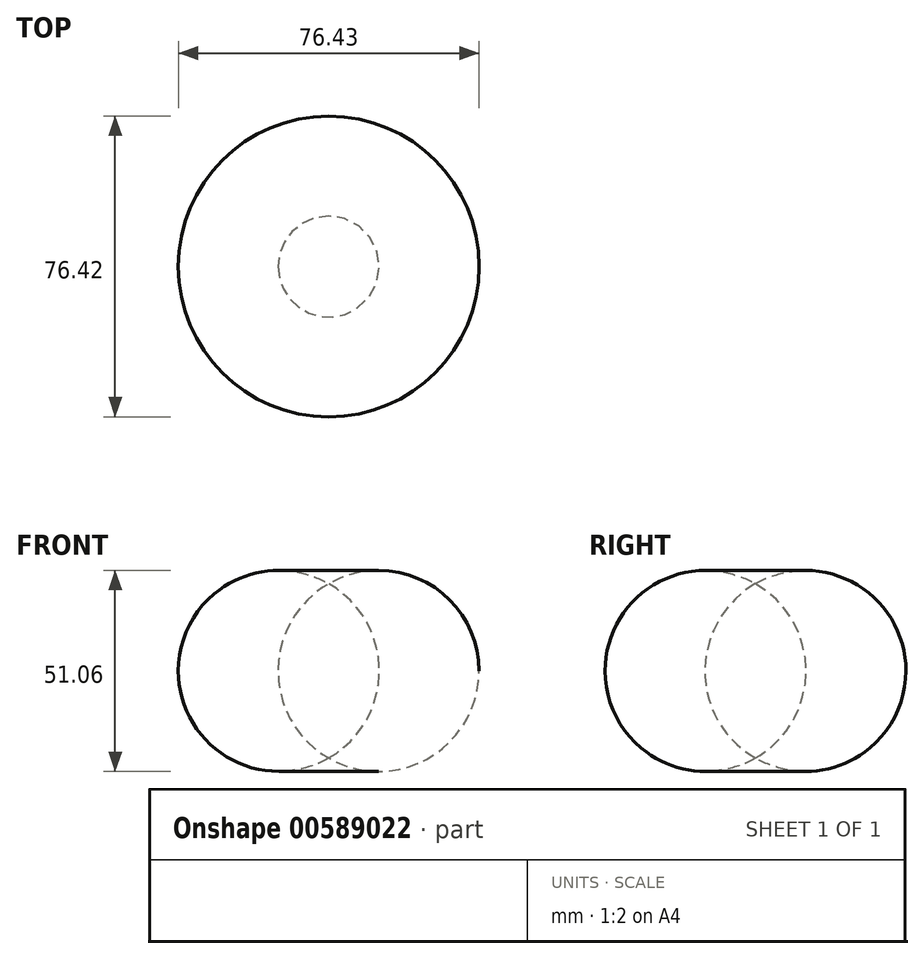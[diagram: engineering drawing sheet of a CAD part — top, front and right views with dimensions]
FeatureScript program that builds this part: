
annotation { "Feature Type Name" : "Feature", "Feature Type Description" : "" }
export const myFeature = defineFeature(function(context is Context, id is Id, definition is map)
    precondition{}
    {
        {
            var Q0;
            Q0=qCreatedBy(makeId("Front.planeOp"),FACE);
            var sketch = newSketch(context, id + "F0", { "sketchPlane" : qUnion([Q0])});
            skArc(sketch, "E0", {"start": v(-19.4, 33.6) * mm, "mid": v(-32.25, 11.44) * mm, "end": v(-19.4, -10.72) * mm});
            skLineSegment(sketch, "E1", {"start": v(-19.4, 33.6) * mm, "end": v(-19.4, -10.72) * mm});
            skSolve(sketch);
        }
        {
            var Q0;
            Q0=makeQuery(id+"F0.imprint","IMPRINT",FACE,{"disambiguationData":[TD([[makeQuery(id+"F0.imprint","IMPRINT",EDGE,{"derivedFrom":sQuery(id+"F0.wireOp",EDGE,"E0")}),1.0]])]});
            var Q1;
            Q1=sQuery(id+"F0.wireOp",EDGE,"E1");
            revolve(context, id + "F1", {"entities" : qUnion([Q0]), "axis" : qUnion([Q1]), "revolveType" : RevolveType.FULL});
        }
    });
